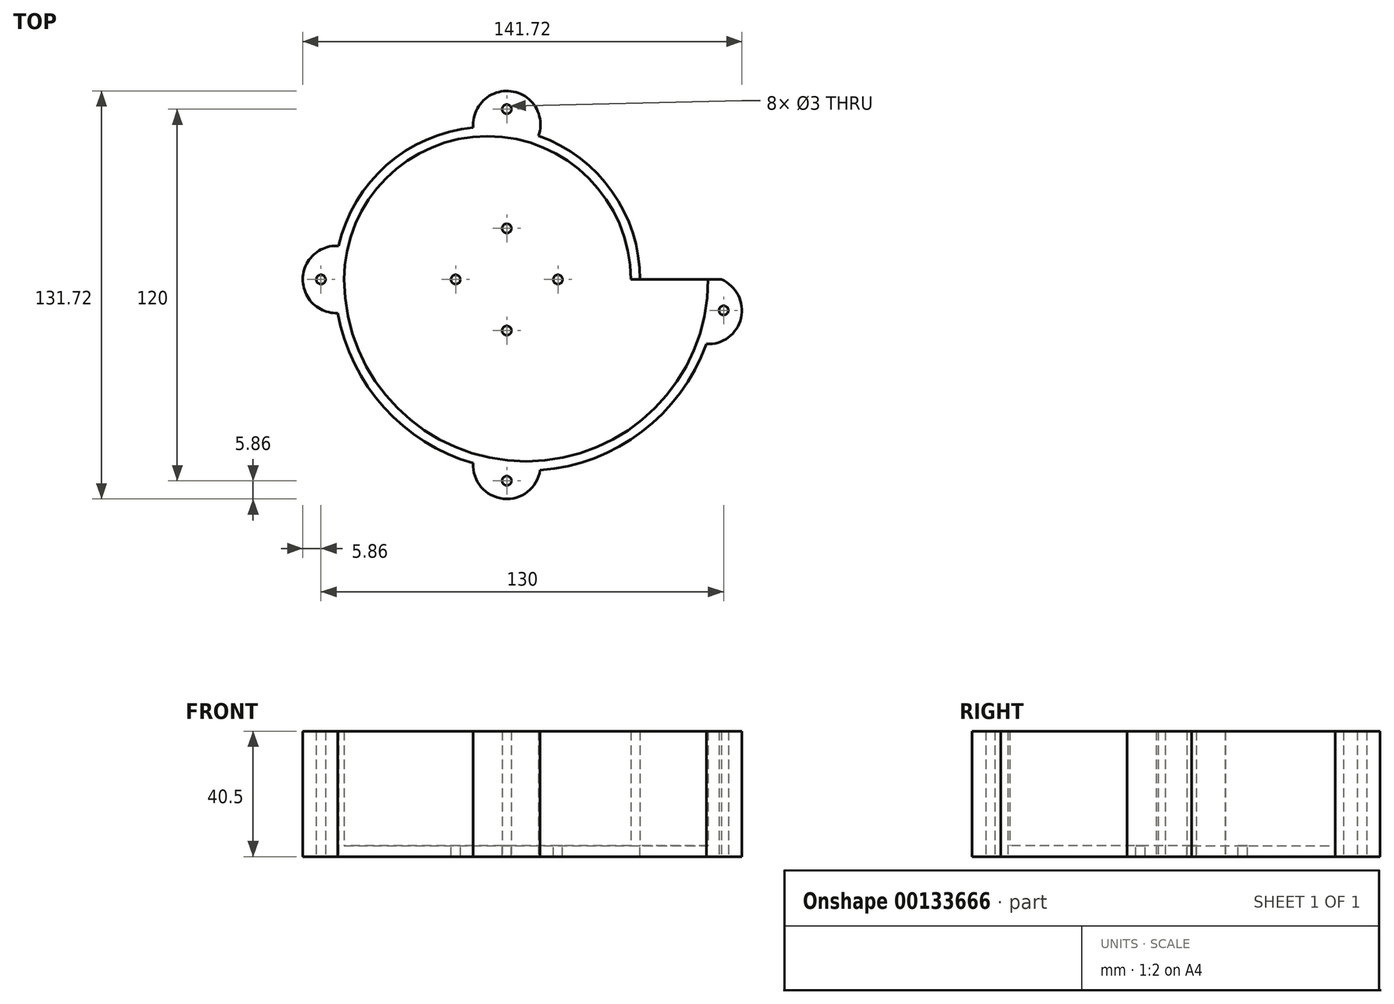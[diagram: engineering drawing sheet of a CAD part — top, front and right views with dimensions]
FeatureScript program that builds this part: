
annotation { "Feature Type Name" : "Feature", "Feature Type Description" : "" }
export const myFeature = defineFeature(function(context is Context, id is Id, definition is map)
    precondition{}
    {
        {
            var Q0;
            Q0=qCreatedBy(makeId("Top.planeOp"),FACE);
            var sketch = newSketch(context, id + "F0", { "sketchPlane" : qUnion([Q0])});
            skCircle(sketch, "E0", {"center": v(0, 0) * mm, "radius": 40 * mm});
            skArc(sketch, "E1", {"start": v(40, 0) * mm, "mid": v(-6.25, 46.25) * mm, "end": v(-52.5, 0) * mm});
            skArc(sketch, "E2", {"start": v(-52.5, 0) * mm, "mid": v(6.25, -58.75) * mm, "end": v(65, 0) * mm});
            skLineSegment(sketch, "E3", {"start": v(0, 0) * mm, "end": v(-6.25, 0) * mm});
            skLineSegment(sketch, "E4", {"start": v(0, 0) * mm, "end": v(6.25, 0) * mm});
            skArc(sketch, "E5.0", {"start": v(-55.5, 0) * mm, "mid": v(6.25, -61.75) * mm, "end": v(68, 0) * mm});
            skArc(sketch, "E5.1", {"start": v(43, 0) * mm, "mid": v(-6.25, 49.25) * mm, "end": v(-55.5, 0) * mm});
            skLineSegment(sketch, "E6", {"start": v(40, 0) * mm, "end": v(43, 0) * mm});
            skLineSegment(sketch, "E7", {"start": v(68, 0) * mm, "end": v(65, 0) * mm});
            skLineSegment(sketch, "E8", {"start": v(65, 0) * mm, "end": v(43, 0) * mm});
            skSolve(sketch);
        }
        {
            var Q0;
            Q0=makeQuery(id+"F0.imprint","IMPRINT",FACE,{"disambiguationData":[TD([[makeQuery(id+"F0.imprint","IMPRINT",EDGE,{"derivedFrom":sQuery(id+"F0.wireOp",EDGE,"E0")}),1.0]])]});
            var Q1;
            Q1=makeQuery(id+"F0.imprint","IMPRINT",FACE,{"disambiguationData":[TD([[makeQuery(id+"F0.imprint","IMPRINT",EDGE,{"derivedFrom":sQuery(id+"F0.wireOp",EDGE,"E0")}),-1.0]])]});
            var Q2;
            Q2=makeQuery(id+"F0.imprint","IMPRINT",FACE,{"disambiguationData":[TD([[makeQuery(id+"F0.imprint","IMPRINT",EDGE,{"derivedFrom":sQuery(id+"F0.wireOp",EDGE,"E1")}),-1.0]])]});
            extrude(context, id + "F1", {"entities" : qUnion([Q0, Q1, Q2]), "oppositeDirection" : true, "depth" : 3.5 * mm});
        }
        {
            var Q0;
            Q0=makeQuery(id+"F0.imprint","IMPRINT",FACE,{"disambiguationData":[TD([[makeQuery(id+"F0.imprint","IMPRINT",EDGE,{"derivedFrom":sQuery(id+"F0.wireOp",EDGE,"E1")}),-1.0]])]});
            extrude(context, id + "F2", {"entities" : qUnion([Q0]), "operationType" : NewBodyOperationType.ADD, "depth" : 37 * mm});
        }
        {
            var Q0;
            Q0=makeQuery(id+"F1.opExtrude","CAP_FACE",FACE,{"disambiguationData":[OSD([sQuery(id+"F0.wireOp",EDGE,"E5.0"),sQuery(id+"F0.wireOp",EDGE,"E5.1"),sQuery(id+"F0.wireOp",EDGE,"E7"),sQuery(id+"F0.wireOp",EDGE,"E8")])],"isStart":true});
            var sketch = newSketch(context, id + "F3", { "sketchPlane" : qUnion([Q0])});
            skLineSegment(sketch, "E9", {"start": v(0, 0) * mm, "end": v(0, 16.5) * mm});
            skLineSegment(sketch, "E10", {"start": v(0, 0) * mm, "end": v(16.5, 0) * mm});
            skLineSegment(sketch, "E11", {"start": v(0, 0) * mm, "end": v(0, -16.5) * mm});
            skLineSegment(sketch, "E12", {"start": v(0, 0) * mm, "end": v(-16.5, 0) * mm});
            skCircle(sketch, "E13", {"center": v(0, 16.5) * mm, "radius": 1.5 * mm});
            skCircle(sketch, "E14", {"center": v(16.5, 0) * mm, "radius": 1.5 * mm});
            skCircle(sketch, "E15", {"center": v(0, -16.5) * mm, "radius": 1.5 * mm});
            skCircle(sketch, "E16", {"center": v(-16.5, 0) * mm, "radius": 1.5 * mm});
            skPoint(sketch, "E17", {"position": v(15, 0) * mm});
            skSolve(sketch);
        }
        {
            var Q0;
            Q0=makeQuery(id+"F3.imprint","IMPRINT",FACE,{"disambiguationData":[TD([[makeQuery(id+"F3.imprint","IMPRINT",EDGE,{"derivedFrom":sQuery(id+"F3.wireOp",EDGE,"E13")}),1.0]])]});
            var Q1;
            Q1=makeQuery(id+"F3.imprint","IMPRINT",FACE,{"disambiguationData":[TD([[makeQuery(id+"F3.imprint","IMPRINT",EDGE,{"derivedFrom":sQuery(id+"F3.wireOp",EDGE,"E14")}),1.0]])]});
            var Q2;
            Q2=makeQuery(id+"F3.imprint","IMPRINT",FACE,{"disambiguationData":[TD([[makeQuery(id+"F3.imprint","IMPRINT",EDGE,{"derivedFrom":sQuery(id+"F3.wireOp",EDGE,"E15")}),1.0]])]});
            var Q3;
            Q3=makeQuery(id+"F3.imprint","IMPRINT",FACE,{"disambiguationData":[TD([[makeQuery(id+"F3.imprint","IMPRINT",EDGE,{"derivedFrom":sQuery(id+"F3.wireOp",EDGE,"E16")}),1.0]])]});
            extrude(context, id + "F4", {"entities" : qUnion([Q0, Q1, Q2, Q3]), "operationType" : NewBodyOperationType.REMOVE, "oppositeDirection" : true, "depth" : 25 * mm});
        }
        {
            var Q0;
            Q0=makeQuery(id+"F1.opExtrude","CAP_FACE",FACE,{"disambiguationData":[OSD([sQuery(id+"F0.wireOp",EDGE,"E5.0"),sQuery(id+"F0.wireOp",EDGE,"E5.1"),sQuery(id+"F0.wireOp",EDGE,"E7"),sQuery(id+"F0.wireOp",EDGE,"E8")])],"isStart":false});
            var sketch = newSketch(context, id + "F5", { "sketchPlane" : qUnion([Q0])});
            skLineSegment(sketch, "E18", {"start": v(0, 0) * mm, "end": v(-60, 0) * mm, "construction": true});
            skLineSegment(sketch, "E19", {"start": v(0, 0) * mm, "end": v(0, 65) * mm, "construction": true});
            skLineSegment(sketch, "E20", {"start": v(0, 0) * mm, "end": v(0, -55) * mm, "construction": true});
            skLineSegment(sketch, "E21", {"start": v(0, 0) * mm, "end": v(35.05, 0) * mm, "construction": true});
            skLineSegment(sketch, "E22", {"start": v(35.05, 0) * mm, "end": v(35.05, 10) * mm, "construction": true});
            skLineSegment(sketch, "E23", {"start": v(35.05, 10) * mm, "end": v(70, 10) * mm, "construction": true});
            skCircle(sketch, "E24", {"center": v(-60, 0) * mm, "radius": 1.5 * mm});
            skCircle(sketch, "E25", {"center": v(0, -55) * mm, "radius": 1.5 * mm});
            skCircle(sketch, "E26", {"center": v(0, 65) * mm, "radius": 1.5 * mm});
            skCircle(sketch, "E27", {"center": v(70, 10) * mm, "radius": 1.5 * mm});
            skCircle(sketch, "E28", {"center": v(-55, 0) * mm, "radius": 10.86 * mm});
            skCircle(sketch, "E29", {"center": v(0, 60) * mm, "radius": 10.86 * mm});
            skCircle(sketch, "E30", {"center": v(65, 10) * mm, "radius": 10.86 * mm});
            skCircle(sketch, "E31", {"center": v(0, -50) * mm, "radius": 10.86 * mm});
            skLineSegment(sketch, "E32", {"start": v(68, 0) * mm, "end": v(69.23, 0) * mm});
            skSolve(sketch);
        }
        {
            var Q0;
            Q0=makeQuery(id+"F5.imprint","IMPRINT",FACE,{"disambiguationData":[TD([[makeQuery(id+"F5.imprint","IMPRINT",EDGE,{"derivedFrom":sQuery(id+"F5.wireOp",EDGE,"E26")}),-1.0]])]});
            var Q1;
            {var subQ0=sQuery(id+"F5.wireOp",EDGE,"E28");var subQ1=makeQuery(id+"F1.opExtrude","CAP_EDGE",EDGE,{"disambiguationData":[OSD([sQuery(id+"F0.wireOp",EDGE,"E5.0")])],"isStart":false});var subQ2=makeQuery(id+"F5.imprint","INTERSECT",VERTEX,{"derivedFrom":[subQ1,subQ0]});Q1=makeQuery(id+"F5.imprint","IMPRINT",FACE,{"disambiguationData":[TD([[makeQuery(id+"F5.imprint","IMPRINT",EDGE,{"disambiguationData":[TD([[subQ2,-1.0]])],"derivedFrom":subQ0}),1.0]])]});}
            var Q2;
            Q2=makeQuery(id+"F5.imprint","IMPRINT",FACE,{"disambiguationData":[TD([[makeQuery(id+"F5.imprint","IMPRINT",EDGE,{"derivedFrom":sQuery(id+"F5.wireOp",EDGE,"E25")}),-1.0]])]});
            var Q3;
            Q3=makeQuery(id+"F5.imprint","IMPRINT",FACE,{"disambiguationData":[TD([[makeQuery(id+"F5.imprint","IMPRINT",EDGE,{"derivedFrom":sQuery(id+"F5.wireOp",EDGE,"E27")}),-1.0]])]});
            extrude(context, id + "F6", {"entities" : qUnion([Q0, Q1, Q2, Q3]), "operationType" : NewBodyOperationType.ADD, "oppositeDirection" : true, "depth" : 40.5 * mm});
        }
    });
